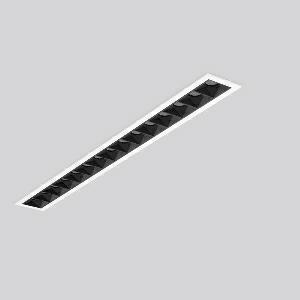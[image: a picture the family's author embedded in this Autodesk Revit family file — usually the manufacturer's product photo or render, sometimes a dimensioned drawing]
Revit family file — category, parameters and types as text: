
# Revit family: beamline_slim_641329_002_1884
name_source: partatom
category: Lighting Fixtures
units: mm (PartAtom-declared; Revit-internal decimal feet)

## family parameters
Cut with Voids When Loaded = No
Host = Face
Light Source = No
Part Type = Normal
Room Calculation Point = No
Round Connector Dimension = Use Diameter
Shared = No

## types (1)
- BEAMLINE SLIM (1 x LED Modul 927, 2700 lm, 2700)
    Apparent Load = 36 VA
    CIE Flux Codes = 100 100 100 100 100
    Color Rendering = 92
    Color Temperature = 2700
    Default Elevation = 1800 mm
    Description = Series: BEAMLINE SLIM
Minimalistic recessed ceiling luminaire for aesthetically sophisticated lighting. Housing: metal, powder-coated. Perfect heat management with an aluminium heat sink. LED light unit with MRS technology: Mini-Reflector-System made of metallised thermoplastic with prismatic black glare-suppressing frame for pleasant glare-free light (RUG < 10). Narrow beam light distribution. Ceiling installation with spring system. Including separate LED converter with connecting cable 450 mm. 
Colour: traffic white, matt (RAL 9016)
Length: 435 mm
Width: 45 mm
Height: 1.5 mm
Cut-out length: 430 mm
Cut-out width: 40 mm
Recess height: 110 mm
Luminaire: recess height: 60 mm
Lamp: LED
Socket: without socket
Colour temperature: 2700K
Colour rendering index (CRI): 90
System power: 36 W
Rated luminous flux: 2700 lm
Luminous efficiency: 75 lm/W
Control gear: Regulated power supply
Protection class: II
Type of protection: IP 20
    Height = 0 mm  [stored 0 ft]
    Lamp = 1 x LED Modul 927
    Lamp Light Flux = 2700 lm
    Lamp count = 1
    Length = 435 mm
    Lifetime = 50000 h
    Luminous efficacy = 75 lm/W
    Manufacturer = RZB
    ModVariant = No
    Model = 641329.002
    Mounting Place = Ceiling
    Mounting Type = Recessed
    Number of Poles = 1
    OnlyDefault = Yes
    Power Factor = 1
    Product Name = BEAMLINE SLIM
    Product group = Recessed LED linear luminaires
    ProductGroupID = 407
    Protection Class = Protection class II
    Protection Degree = IP 20
    RLX_Detail_Level = 1
    RLX_Emergency_Light_Flux = 0 lm
    RLX_Emergency_Type = 0
    RLX_Emergency_Type_DB = No
    RlxData = <blob elided: 18797 chars, md5=d902953a>
    Socket = socket
    Standby Power = 0 W
    System Light Flux = 2700 lm
    System Power = 36 W
    Type Comments = Product without accessories
    Type Image = 641329.002.jpg
    URL = http://relux.com
    VarID = ---
    Voltage = 230 V
    Voltage Range = 220-240 V
    Weight = 0.00 kg
    Width = 45 mm

note: [stored X ft] marks values corroborated as IEEE doubles in the binary element streams (Revit-internal decimal feet)

## geometry (parser evidence)
native form markers: Blend x4, Sweep x10
no freeform markers — native parametric forms only
